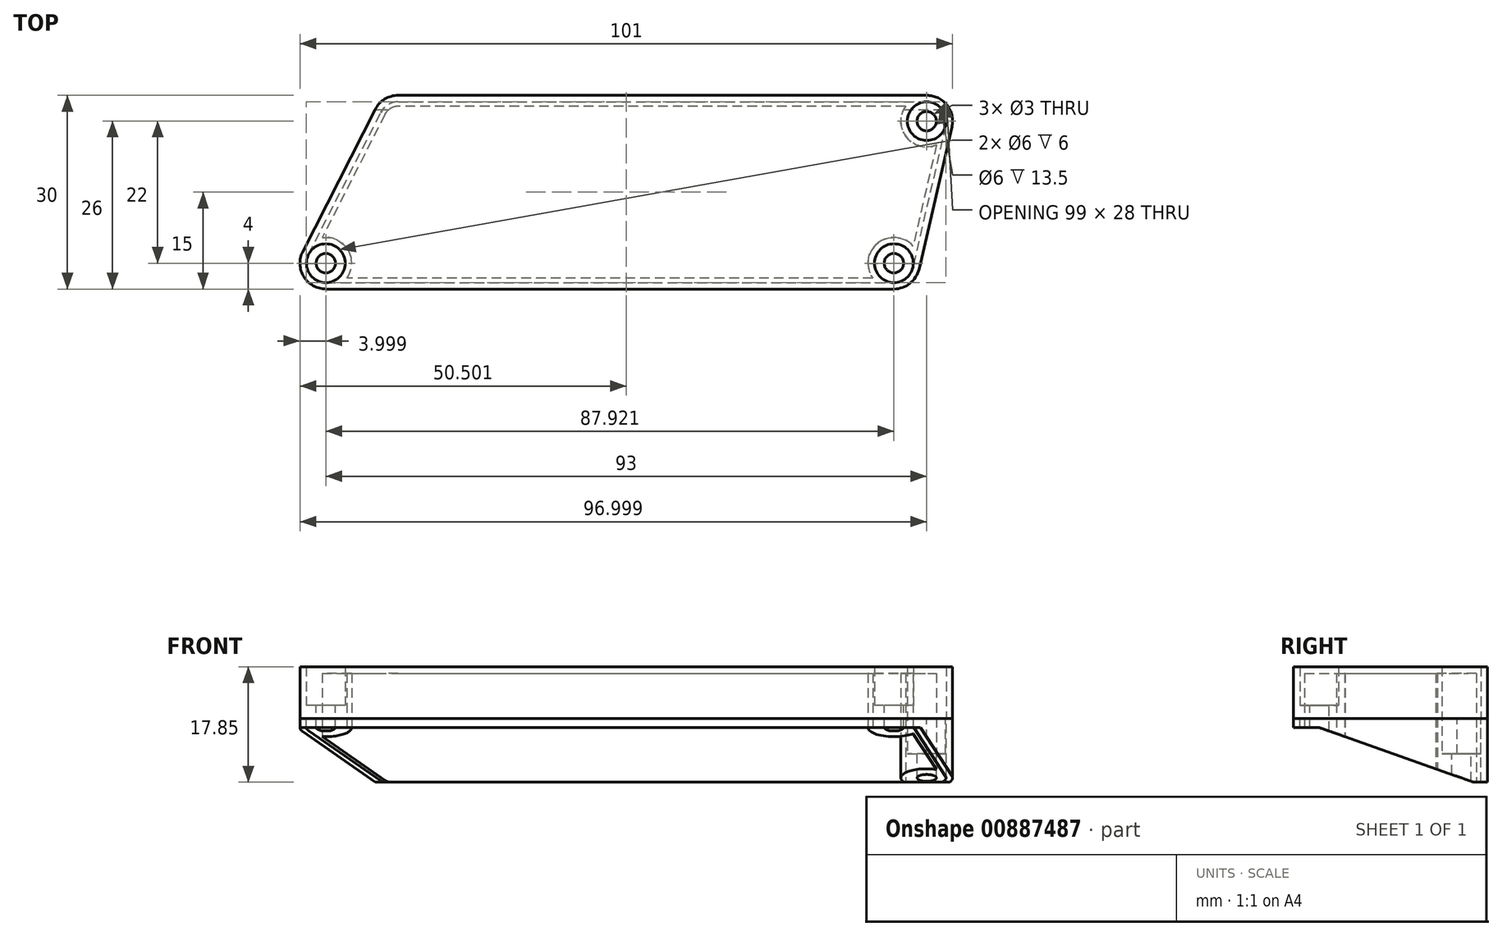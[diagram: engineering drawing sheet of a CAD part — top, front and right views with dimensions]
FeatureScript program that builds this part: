
annotation { "Feature Type Name" : "Feature", "Feature Type Description" : "" }
export const myFeature = defineFeature(function(context is Context, id is Id, definition is map)
    precondition{}
    {
        {
            var Q0;
            Q0=qCreatedBy(makeId("Top.planeOp"),FACE);
            var sketch = newSketch(context, id + "F0", { "sketchPlane" : qUnion([Q0])});
            skLineSegment(sketch, "E0.bottom", {"start": v(52.28, -15) * mm, "end": v(-52.28, -15) * mm, "construction": true});
            skLineSegment(sketch, "E0.top", {"start": v(52.28, 15) * mm, "end": v(-52.28, 15) * mm, "construction": true});
            skLineSegment(sketch, "E0.left", {"start": v(52.28, -15) * mm, "end": v(52.28, 15) * mm, "construction": true});
            skLineSegment(sketch, "E0.right", {"start": v(-52.28, -15) * mm, "end": v(-52.28, 15) * mm, "construction": true});
            skPoint(sketch, "E0.middle", {"position": v(0, 0) * mm});
            skLineSegment(sketch, "E1", {"start": v(-52.28, -15) * mm, "end": v(-37, 15) * mm});
            skLineSegment(sketch, "E2", {"start": v(52.28, 15) * mm, "end": v(45.35, -15) * mm});
            skLineSegment(sketch, "E3", {"start": v(-37, 15) * mm, "end": v(52.28, 15) * mm});
            skLineSegment(sketch, "E4", {"start": v(45.35, -15) * mm, "end": v(-52.28, -15) * mm});
            skCircle(sketch, "E5", {"center": v(-45.75, -11) * mm, "radius": 3 * mm});
            skCircle(sketch, "E6", {"center": v(-45.75, -11) * mm, "radius": 4 * mm});
            skCircle(sketch, "E7", {"center": v(-45.75, -11) * mm, "radius": 1.5 * mm});
            skCircle(sketch, "E8", {"center": v(-34.54, 11) * mm, "radius": 3 * mm});
            skCircle(sketch, "E9", {"center": v(-34.54, 11) * mm, "radius": 4 * mm});
            skCircle(sketch, "E10", {"center": v(-34.54, 11) * mm, "radius": 1.5 * mm});
            skCircle(sketch, "E11", {"center": v(47.25, 11) * mm, "radius": 3 * mm});
            skCircle(sketch, "E12", {"center": v(47.25, 11) * mm, "radius": 4 * mm});
            skCircle(sketch, "E13", {"center": v(47.25, 11) * mm, "radius": 1.5 * mm});
            skCircle(sketch, "E14", {"center": v(42.17, -11) * mm, "radius": 3 * mm});
            skCircle(sketch, "E15", {"center": v(42.17, -11) * mm, "radius": 4 * mm});
            skCircle(sketch, "E16", {"center": v(42.17, -11) * mm, "radius": 1.5 * mm});
            skLineSegment(sketch, "E17", {"start": v(50.17, 10.33) * mm, "end": v(45.1, -11.67) * mm});
            skLineSegment(sketch, "E18", {"start": v(-45.75, -14) * mm, "end": v(42.17, -14) * mm});
            skLineSegment(sketch, "E19", {"start": v(-48.42, -9.64) * mm, "end": v(-37.21, 12.36) * mm});
            skLineSegment(sketch, "E20", {"start": v(-34.54, 14) * mm, "end": v(47.25, 14) * mm});
            skLineSegment(sketch, "E21", {"start": v(-42.48, -13.3) * mm, "end": v(38.9, -13.3) * mm});
            skLineSegment(sketch, "E22", {"start": v(45.15, -8.33) * mm, "end": v(48.75, 7.3) * mm});
            skLineSegment(sketch, "E23", {"start": v(-31.27, 13.3) * mm, "end": v(43.98, 13.3) * mm});
            skLineSegment(sketch, "E24", {"start": v(-46.31, -7.04) * mm, "end": v(-38.08, 9.13) * mm});
            skLineSegment(sketch, "E25", {"start": v(-38.08, 9.13) * mm, "end": v(-37.46, 10.33) * mm});
            skLineSegment(sketch, "E26", {"start": v(-31.27, 13.3) * mm, "end": v(-32.61, 13.3) * mm});
            skLineSegment(sketch, "E27", {"start": v(43.98, 13.3) * mm, "end": v(45.32, 13.3) * mm});
            skLineSegment(sketch, "E28", {"start": v(48.75, 7.3) * mm, "end": v(49.06, 8.6) * mm});
            skLineSegment(sketch, "E29", {"start": v(45.15, -8.33) * mm, "end": v(44.84, -9.64) * mm});
            skLineSegment(sketch, "E30", {"start": v(38.9, -13.3) * mm, "end": v(40.24, -13.3) * mm});
            skLineSegment(sketch, "E31", {"start": v(-42.48, -13.3) * mm, "end": v(-43.82, -13.3) * mm});
            skLineSegment(sketch, "E32", {"start": v(-46.31, -7.04) * mm, "end": v(-46.93, -8.24) * mm});
            skLineSegment(sketch, "E33", {"start": v(-37.46, 10.33) * mm, "end": v(-35.95, 13.3) * mm});
            skLineSegment(sketch, "E34", {"start": v(-35.95, 13.3) * mm, "end": v(-32.61, 13.3) * mm});
            skCircle(sketch, "E35", {"center": v(-34.54, 11) * mm, "radius": 2.3 * mm});
            skLineSegment(sketch, "E36", {"start": v(-49.75, -15) * mm, "end": v(-49.75, 15) * mm, "construction": true});
            skLineSegment(sketch, "E37", {"start": v(51.25, 15) * mm, "end": v(51.25, -15) * mm, "construction": true});
            skSolve(sketch);
        }
        {
            var Q0;
            {var subQ2=sQuery(id+"F0.wireOp",EDGE,"E17");var subQ7=sQuery(id+"F0.wireOp",EDGE,"E14");var subQ8=makeQuery(id+"F0.imprint","INTERSECT",VERTEX,{"derivedFrom":[subQ7,subQ2]});Q0=makeQuery(id+"F0.imprint","IMPRINT",FACE,{"disambiguationData":[TD([[makeQuery(id+"F0.imprint","IMPRINT",EDGE,{"disambiguationData":[TD([[subQ8,1.0]])],"derivedFrom":subQ7}),-1.0]])]});}
            var Q1;
            {var subQ5=sQuery(id+"F0.wireOp",EDGE,"E14");var subQ7=sQuery(id+"F0.wireOp",EDGE,"E17");var subQ9=makeQuery(id+"F0.imprint","INTERSECT",VERTEX,{"derivedFrom":[subQ5,subQ7]});Q1=makeQuery(id+"F0.imprint","IMPRINT",FACE,{"disambiguationData":[TD([[makeQuery(id+"F0.imprint","IMPRINT",EDGE,{"disambiguationData":[TD([[subQ9,-1.0]])],"derivedFrom":subQ5}),-1.0]])]});}
            var Q2;
            Q2=makeQuery(id+"F0.imprint","IMPRINT",FACE,{"disambiguationData":[TD([[makeQuery(id+"F0.imprint","IMPRINT",EDGE,{"derivedFrom":sQuery(id+"F0.wireOp",EDGE,"E16")}),-1.0]])]});
            var Q3;
            Q3=makeQuery(id+"F0.imprint","IMPRINT",FACE,{"disambiguationData":[TD([[makeQuery(id+"F0.imprint","IMPRINT",EDGE,{"derivedFrom":sQuery(id+"F0.wireOp",EDGE,"E13")}),-1.0]])]});
            var Q4;
            {var subQ0=sQuery(id+"F0.wireOp",EDGE,"E6");var subQ1=sQuery(id+"F0.wireOp",EDGE,"E1");var subQ2=makeQuery(id+"F0.imprint","INTERSECT",VERTEX,{"derivedFrom":[subQ1,subQ0]});Q4=makeQuery(id+"F0.imprint","IMPRINT",FACE,{"disambiguationData":[TD([[makeQuery(id+"F0.imprint","IMPRINT",EDGE,{"disambiguationData":[TD([[subQ2,-1.0]])],"derivedFrom":subQ1}),-1.0]])]});}
            var Q5;
            {var subQ0=sQuery(id+"F0.wireOp",EDGE,"E9");var subQ1=sQuery(id+"F0.wireOp",EDGE,"E3");var subQ2=makeQuery(id+"F0.imprint","INTERSECT",VERTEX,{"derivedFrom":[subQ1,subQ0]});Q5=makeQuery(id+"F0.imprint","IMPRINT",FACE,{"disambiguationData":[TD([[makeQuery(id+"F0.imprint","IMPRINT",EDGE,{"disambiguationData":[TD([[subQ2,-1.0]])],"derivedFrom":subQ1}),-1.0]])]});}
            var Q6;
            {var subQ0=sQuery(id+"F0.wireOp",EDGE,"E12");var subQ1=sQuery(id+"F0.wireOp",EDGE,"E2");var subQ2=makeQuery(id+"F0.imprint","INTERSECT",VERTEX,{"derivedFrom":[subQ1,subQ0]});Q6=makeQuery(id+"F0.imprint","IMPRINT",FACE,{"disambiguationData":[TD([[makeQuery(id+"F0.imprint","IMPRINT",EDGE,{"disambiguationData":[TD([[subQ2,-1.0]])],"derivedFrom":subQ1}),-1.0]])]});}
            var Q7;
            {var subQ0=sQuery(id+"F0.wireOp",EDGE,"E22");Q7=makeQuery(id+"F0.imprint","IMPRINT",FACE,{"disambiguationData":[TD([[makeQuery(id+"F0.imprint","IMPRINT",EDGE,{"derivedFrom":subQ0}),-1.0]])]});}
            var Q8;
            {var subQ0=sQuery(id+"F0.wireOp",EDGE,"E24");Q8=makeQuery(id+"F0.imprint","IMPRINT",FACE,{"disambiguationData":[TD([[makeQuery(id+"F0.imprint","IMPRINT",EDGE,{"derivedFrom":subQ0}),1.0]])]});}
            var Q9;
            Q9=makeQuery(id+"F0.imprint","IMPRINT",FACE,{"disambiguationData":[TD([[makeQuery(id+"F0.imprint","IMPRINT",EDGE,{"derivedFrom":sQuery(id+"F0.wireOp",EDGE,"E16")}),1.0]])]});
            var Q10;
            Q10=makeQuery(id+"F0.imprint","IMPRINT",FACE,{"disambiguationData":[TD([[makeQuery(id+"F0.imprint","IMPRINT",EDGE,{"derivedFrom":sQuery(id+"F0.wireOp",EDGE,"E13")}),1.0]])]});
            var Q11;
            {var subQ5=sQuery(id+"F0.wireOp",EDGE,"E18");var subQ7=sQuery(id+"F0.wireOp",EDGE,"E5");var subQ8=makeQuery(id+"F0.imprint","INTERSECT",VERTEX,{"derivedFrom":[subQ7,subQ5]});Q11=makeQuery(id+"F0.imprint","IMPRINT",FACE,{"disambiguationData":[TD([[makeQuery(id+"F0.imprint","IMPRINT",EDGE,{"disambiguationData":[TD([[subQ8,1.0]])],"derivedFrom":subQ7}),-1.0]])]});}
            var Q12;
            Q12=makeQuery(id+"F0.imprint","IMPRINT",FACE,{"disambiguationData":[TD([[makeQuery(id+"F0.imprint","IMPRINT",EDGE,{"derivedFrom":sQuery(id+"F0.wireOp",EDGE,"E7")}),-1.0]])]});
            var Q13;
            Q13=makeQuery(id+"F0.imprint","IMPRINT",FACE,{"disambiguationData":[TD([[makeQuery(id+"F0.imprint","IMPRINT",EDGE,{"derivedFrom":sQuery(id+"F0.wireOp",EDGE,"E7")}),1.0]])]});
            var Q14;
            {var subQ5=sQuery(id+"F0.wireOp",EDGE,"E18");var subQ7=sQuery(id+"F0.wireOp",EDGE,"E5");var subQ8=makeQuery(id+"F0.imprint","INTERSECT",VERTEX,{"derivedFrom":[subQ7,subQ5]});Q14=makeQuery(id+"F0.imprint","IMPRINT",FACE,{"disambiguationData":[TD([[makeQuery(id+"F0.imprint","IMPRINT",EDGE,{"disambiguationData":[TD([[subQ8,-1.0]])],"derivedFrom":subQ7}),-1.0]])]});}
            var Q15;
            {var subQ0=sQuery(id+"F0.wireOp",EDGE,"E21");Q15=makeQuery(id+"F0.imprint","IMPRINT",FACE,{"disambiguationData":[TD([[makeQuery(id+"F0.imprint","IMPRINT",EDGE,{"derivedFrom":subQ0}),-1.0]])]});}
            var Q16;
            {var subQ0=sQuery(id+"F0.wireOp",EDGE,"E15");var subQ1=sQuery(id+"F0.wireOp",EDGE,"E4");var subQ2=makeQuery(id+"F0.imprint","INTERSECT",VERTEX,{"derivedFrom":[subQ1,subQ0]});Q16=makeQuery(id+"F0.imprint","IMPRINT",FACE,{"disambiguationData":[TD([[makeQuery(id+"F0.imprint","IMPRINT",EDGE,{"disambiguationData":[TD([[subQ2,-1.0]])],"derivedFrom":subQ1}),-1.0]])]});}
            var Q17;
            {var subQ5=sQuery(id+"F0.wireOp",EDGE,"E19");var subQ6=sQuery(id+"F0.wireOp",EDGE,"E8");var subQ7=makeQuery(id+"F0.imprint","INTERSECT",VERTEX,{"derivedFrom":[subQ6,subQ5]});Q17=makeQuery(id+"F0.imprint","IMPRINT",FACE,{"disambiguationData":[TD([[makeQuery(id+"F0.imprint","IMPRINT",EDGE,{"disambiguationData":[TD([[subQ7,-1.0]])],"derivedFrom":subQ6}),-1.0]])]});}
            var Q18;
            {var subQ5=sQuery(id+"F0.wireOp",EDGE,"E17");var subQ7=sQuery(id+"F0.wireOp",EDGE,"E11");var subQ8=makeQuery(id+"F0.imprint","INTERSECT",VERTEX,{"derivedFrom":[subQ7,subQ5]});Q18=makeQuery(id+"F0.imprint","IMPRINT",FACE,{"disambiguationData":[TD([[makeQuery(id+"F0.imprint","IMPRINT",EDGE,{"disambiguationData":[TD([[subQ8,1.0]])],"derivedFrom":subQ7}),-1.0]])]});}
            var Q19;
            {var subQ3=sQuery(id+"F0.wireOp",EDGE,"E17");var subQ4=sQuery(id+"F0.wireOp",EDGE,"E11");var subQ5=makeQuery(id+"F0.imprint","INTERSECT",VERTEX,{"derivedFrom":[subQ4,subQ3]});Q19=makeQuery(id+"F0.imprint","IMPRINT",FACE,{"disambiguationData":[TD([[makeQuery(id+"F0.imprint","IMPRINT",EDGE,{"disambiguationData":[TD([[subQ5,-1.0]])],"derivedFrom":subQ4}),-1.0]])]});}
            var Q20;
            {var subQ5=sQuery(id+"F0.wireOp",EDGE,"E8");var subQ7=sQuery(id+"F0.wireOp",EDGE,"E19");var subQ9=makeQuery(id+"F0.imprint","INTERSECT",VERTEX,{"derivedFrom":[subQ5,subQ7]});Q20=makeQuery(id+"F0.imprint","IMPRINT",FACE,{"disambiguationData":[TD([[makeQuery(id+"F0.imprint","IMPRINT",EDGE,{"disambiguationData":[TD([[subQ9,1.0]])],"derivedFrom":subQ5}),-1.0]])]});}
            var Q21;
            {var subQ0=sQuery(id+"F0.wireOp",EDGE,"E23");Q21=makeQuery(id+"F0.imprint","IMPRINT",FACE,{"disambiguationData":[TD([[makeQuery(id+"F0.imprint","IMPRINT",EDGE,{"derivedFrom":subQ0}),1.0]])]});}
            var Q22;
            {var subQ3=sQuery(id+"F0.wireOp",EDGE,"E26");Q22=makeQuery(id+"F0.imprint","IMPRINT",FACE,{"disambiguationData":[TD([[makeQuery(id+"F0.imprint","IMPRINT",EDGE,{"derivedFrom":subQ3}),-1.0]])]});}
            var Q23;
            {var subQ3=sQuery(id+"F0.wireOp",EDGE,"E32");Q23=makeQuery(id+"F0.imprint","IMPRINT",FACE,{"disambiguationData":[TD([[makeQuery(id+"F0.imprint","IMPRINT",EDGE,{"derivedFrom":subQ3}),-1.0]])]});}
            var Q24;
            {var subQ0=sQuery(id+"F0.wireOp",EDGE,"E31");Q24=makeQuery(id+"F0.imprint","IMPRINT",FACE,{"disambiguationData":[TD([[makeQuery(id+"F0.imprint","IMPRINT",EDGE,{"derivedFrom":subQ0}),-1.0]])]});}
            var Q25;
            {var subQ0=sQuery(id+"F0.wireOp",EDGE,"E27");Q25=makeQuery(id+"F0.imprint","IMPRINT",FACE,{"disambiguationData":[TD([[makeQuery(id+"F0.imprint","IMPRINT",EDGE,{"derivedFrom":subQ0}),-1.0]])]});}
            var Q26;
            {var subQ3=sQuery(id+"F0.wireOp",EDGE,"E27");Q26=makeQuery(id+"F0.imprint","IMPRINT",FACE,{"disambiguationData":[TD([[makeQuery(id+"F0.imprint","IMPRINT",EDGE,{"derivedFrom":subQ3}),1.0]])]});}
            var Q27;
            {var subQ0=sQuery(id+"F0.wireOp",EDGE,"E29");Q27=makeQuery(id+"F0.imprint","IMPRINT",FACE,{"disambiguationData":[TD([[makeQuery(id+"F0.imprint","IMPRINT",EDGE,{"derivedFrom":subQ0}),-1.0]])]});}
            var Q28;
            {var subQ3=sQuery(id+"F0.wireOp",EDGE,"E30");Q28=makeQuery(id+"F0.imprint","IMPRINT",FACE,{"disambiguationData":[TD([[makeQuery(id+"F0.imprint","IMPRINT",EDGE,{"derivedFrom":subQ3}),-1.0]])]});}
            var Q29;
            {var subQ1=sQuery(id+"F0.wireOp",EDGE,"E8");var subQ5=makeQuery(id+"F0.imprint","INTERSECT",VERTEX,{"derivedFrom":[subQ1,sQuery(id+"F0.wireOp",EDGE,"E19")]});Q29=makeQuery(id+"F0.imprint","IMPRINT",FACE,{"disambiguationData":[TD([[makeQuery(id+"F0.imprint","IMPRINT",EDGE,{"disambiguationData":[TD([[subQ5,1.0]])],"derivedFrom":subQ1}),1.0]])]});}
            var Q30;
            {var subQ0=sQuery(id+"F0.wireOp",EDGE,"E34");var subQ1=sQuery(id+"F0.wireOp",EDGE,"E33");var subQ2=makeQuery(id+"F0.imprint","INTERSECT",VERTEX,{"derivedFrom":[subQ1,subQ0]});Q30=makeQuery(id+"F0.imprint","IMPRINT",FACE,{"disambiguationData":[TD([[makeQuery(id+"F0.imprint","IMPRINT",EDGE,{"disambiguationData":[TD([[subQ2,1.0]])],"derivedFrom":subQ1}),-1.0]])]});}
            extrude(context, id + "F1", {"entities" : qUnion([Q0, Q1, Q2, Q3, Q4, Q5, Q6, Q7, Q8, Q9, Q10, Q11, Q12, Q13, Q14, Q15, Q16, Q17, Q18, Q19, Q20, Q21, Q22, Q23, Q24, Q25, Q26, Q27, Q28, Q29, Q30]), "depth" : 8 * mm, "offsetDistance" : 25 * mm});
        }
        {
            var Q0;
            {var subQ0=sQuery(id+"F0.wireOp",EDGE,"E21");Q0=makeQuery(id+"F0.imprint","IMPRINT",FACE,{"disambiguationData":[TD([[makeQuery(id+"F0.imprint","IMPRINT",EDGE,{"derivedFrom":subQ0}),1.0]])]});}
            var Q1;
            {var subQ0=sQuery(id+"F0.wireOp",EDGE,"E33");var subQ5=sQuery(id+"F0.wireOp",EDGE,"E35");var subQ6=makeQuery(id+"F0.imprint","INTERSECT",VERTEX,{"derivedFrom":[subQ0,subQ5]});Q1=makeQuery(id+"F0.imprint","IMPRINT",FACE,{"disambiguationData":[TD([[makeQuery(id+"F0.imprint","IMPRINT",EDGE,{"disambiguationData":[TD([[subQ6,-1.0]])],"derivedFrom":subQ5}),-1.0]])]});}
            var Q2;
            Q2=makeQuery(id+"F0.imprint","IMPRINT",FACE,{"disambiguationData":[TD([[makeQuery(id+"F0.imprint","IMPRINT",EDGE,{"derivedFrom":sQuery(id+"F0.wireOp",EDGE,"E10")}),-1.0]])]});
            var Q3;
            Q3=makeQuery(id+"F0.imprint","IMPRINT",FACE,{"disambiguationData":[TD([[makeQuery(id+"F0.imprint","IMPRINT",EDGE,{"derivedFrom":sQuery(id+"F0.wireOp",EDGE,"E10")}),1.0]])]});
            var Q4;
            {var subQ0=sQuery(id+"F0.wireOp",EDGE,"E25");Q4=makeQuery(id+"F0.imprint","IMPRINT",FACE,{"disambiguationData":[TD([[makeQuery(id+"F0.imprint","IMPRINT",EDGE,{"derivedFrom":subQ0}),-1.0]])]});}
            extrude(context, id + "F2", {"entities" : qUnion([Q0, Q1, Q2, Q3, Q4]), "operationType" : NewBodyOperationType.ADD, "depth" : 8 * mm, "offsetDistance" : 25 * mm, "hasSecondDirection" : true, "secondDirectionOppositeDirection" : false, "secondDirectionDepth" : 7 * mm});
        }
        {
            var Q0;
            {var subQ4=sQuery(id+"F0.wireOp",EDGE,"E14");var subQ7=sQuery(id+"F0.wireOp",EDGE,"E17");var subQ9=makeQuery(id+"F0.imprint","INTERSECT",VERTEX,{"derivedFrom":[subQ4,subQ7]});Q0=makeQuery(id+"F0.imprint","IMPRINT",FACE,{"disambiguationData":[TD([[makeQuery(id+"F0.imprint","IMPRINT",EDGE,{"disambiguationData":[TD([[subQ9,-1.0]])],"derivedFrom":subQ4}),-1.0]])]});}
            var Q1;
            {var subQ0=sQuery(id+"F0.wireOp",EDGE,"E9");var subQ6=sQuery(id+"F0.wireOp",EDGE,"sEmSDasX-VnLR-kRRF-FZfv-y3YDyhKKrgE7");var subQ8=makeQuery(id+"F0.imprint","INTERSECT",VERTEX,{"disambiguationData":[OD(0.0)],"derivedFrom":[subQ6,subQ0]});Q1=makeQuery(id+"F0.imprint","IMPRINT",FACE,{"disambiguationData":[TD([[makeQuery(id+"F0.imprint","IMPRINT",EDGE,{"disambiguationData":[TD([[subQ8,-1.0]])],"derivedFrom":subQ6}),1.0]])]});}
            var Q2;
            {var subQ0=sQuery(id+"F0.wireOp",EDGE,"E9");var subQ2=sQuery(id+"F0.wireOp",EDGE,"sEmSDasX-VnLR-kRRF-FZfv-y3YDyhKKrgE7");var subQ3=makeQuery(id+"F0.imprint","INTERSECT",VERTEX,{"disambiguationData":[OD(0.0)],"derivedFrom":[subQ2,subQ0]});Q2=makeQuery(id+"F0.imprint","IMPRINT",FACE,{"disambiguationData":[TD([[makeQuery(id+"F0.imprint","IMPRINT",EDGE,{"disambiguationData":[TD([[subQ3,-1.0]])],"derivedFrom":subQ2}),-1.0]])]});}
            var Q3;
            {var subQ0=sQuery(id+"F0.wireOp",EDGE,"E6");var subQ2=sQuery(id+"F0.wireOp",EDGE,"s6BABxoF-F3zb-I8wc-I3Xw-FraqOPEOQCRA");var subQ3=makeQuery(id+"F0.imprint","INTERSECT",VERTEX,{"disambiguationData":[OD(0.0)],"derivedFrom":[subQ2,subQ0]});Q3=makeQuery(id+"F0.imprint","IMPRINT",FACE,{"disambiguationData":[TD([[makeQuery(id+"F0.imprint","IMPRINT",EDGE,{"disambiguationData":[TD([[subQ3,-1.0]])],"derivedFrom":subQ2}),-1.0]])]});}
            var Q4;
            {var subQ0=sQuery(id+"F0.wireOp",EDGE,"E6");var subQ2=sQuery(id+"F0.wireOp",EDGE,"s6BABxoF-F3zb-I8wc-I3Xw-FraqOPEOQCRA");var subQ3=makeQuery(id+"F0.imprint","INTERSECT",VERTEX,{"disambiguationData":[OD(0.0)],"derivedFrom":[subQ2,subQ0]});Q4=makeQuery(id+"F0.imprint","IMPRINT",FACE,{"disambiguationData":[TD([[makeQuery(id+"F0.imprint","IMPRINT",EDGE,{"disambiguationData":[TD([[subQ3,-1.0]])],"derivedFrom":subQ2}),1.0]])]});}
            var Q5;
            {var subQ0=sQuery(id+"F0.wireOp",EDGE,"E12");var subQ3=sQuery(id+"F0.wireOp",EDGE,"MlNcj02m-OnEw-u7mJ-xsQt-vaGhrOIsEcpA");var subQ4=makeQuery(id+"F0.imprint","INTERSECT",VERTEX,{"disambiguationData":[OD(0.0)],"derivedFrom":[subQ3,subQ0]});Q5=makeQuery(id+"F0.imprint","IMPRINT",FACE,{"disambiguationData":[TD([[makeQuery(id+"F0.imprint","IMPRINT",EDGE,{"disambiguationData":[TD([[subQ4,-1.0]])],"derivedFrom":subQ3}),-1.0]])]});}
            var Q6;
            {var subQ0=sQuery(id+"F0.wireOp",EDGE,"E12");var subQ1=sQuery(id+"F0.wireOp",EDGE,"MlNcj02m-OnEw-u7mJ-xsQt-vaGhrOIsEcpA");var subQ2=makeQuery(id+"F0.imprint","INTERSECT",VERTEX,{"disambiguationData":[OD(0.0)],"derivedFrom":[subQ1,subQ0]});Q6=makeQuery(id+"F0.imprint","IMPRINT",FACE,{"disambiguationData":[TD([[makeQuery(id+"F0.imprint","IMPRINT",EDGE,{"disambiguationData":[TD([[subQ2,-1.0]])],"derivedFrom":subQ1}),1.0]])]});}
            var Q7;
            {var subQ0=sQuery(id+"F0.wireOp",EDGE,"E5");var subQ2=sQuery(id+"F0.wireOp",EDGE,"s6BABxoF-F3zb-I8wc-I3Xw-FraqOPEOQCRA");var subQ7=makeQuery(id+"F0.imprint","INTERSECT",VERTEX,{"disambiguationData":[OD(0.0)],"derivedFrom":[subQ2,subQ0]});Q7=makeQuery(id+"F0.imprint","IMPRINT",FACE,{"disambiguationData":[TD([[makeQuery(id+"F0.imprint","IMPRINT",EDGE,{"disambiguationData":[TD([[subQ7,-1.0]])],"derivedFrom":subQ2}),1.0]])]});}
            var Q8;
            {var subQ0=sQuery(id+"F0.wireOp",EDGE,"E5");var subQ2=sQuery(id+"F0.wireOp",EDGE,"s6BABxoF-F3zb-I8wc-I3Xw-FraqOPEOQCRA");var subQ7=makeQuery(id+"F0.imprint","INTERSECT",VERTEX,{"disambiguationData":[OD(0.0)],"derivedFrom":[subQ2,subQ0]});Q8=makeQuery(id+"F0.imprint","IMPRINT",FACE,{"disambiguationData":[TD([[makeQuery(id+"F0.imprint","IMPRINT",EDGE,{"disambiguationData":[TD([[subQ7,-1.0]])],"derivedFrom":subQ2}),-1.0]])]});}
            var Q9;
            {var subQ0=sQuery(id+"F0.wireOp",EDGE,"E8");var subQ2=sQuery(id+"F0.wireOp",EDGE,"sEmSDasX-VnLR-kRRF-FZfv-y3YDyhKKrgE7");var subQ4=makeQuery(id+"F0.imprint","INTERSECT",VERTEX,{"disambiguationData":[OD(0.0)],"derivedFrom":[subQ2,subQ0]});Q9=makeQuery(id+"F0.imprint","IMPRINT",FACE,{"disambiguationData":[TD([[makeQuery(id+"F0.imprint","IMPRINT",EDGE,{"disambiguationData":[TD([[subQ4,-1.0]])],"derivedFrom":subQ2}),-1.0]])]});}
            var Q10;
            {var subQ0=sQuery(id+"F0.wireOp",EDGE,"E8");var subQ2=sQuery(id+"F0.wireOp",EDGE,"sEmSDasX-VnLR-kRRF-FZfv-y3YDyhKKrgE7");var subQ3=makeQuery(id+"F0.imprint","INTERSECT",VERTEX,{"disambiguationData":[OD(0.0)],"derivedFrom":[subQ2,subQ0]});Q10=makeQuery(id+"F0.imprint","IMPRINT",FACE,{"disambiguationData":[TD([[makeQuery(id+"F0.imprint","IMPRINT",EDGE,{"disambiguationData":[TD([[subQ3,-1.0]])],"derivedFrom":subQ2}),1.0]])]});}
            var Q11;
            {var subQ0=sQuery(id+"F0.wireOp",EDGE,"E11");var subQ1=sQuery(id+"F0.wireOp",EDGE,"MlNcj02m-OnEw-u7mJ-xsQt-vaGhrOIsEcpA");var subQ2=makeQuery(id+"F0.imprint","INTERSECT",VERTEX,{"disambiguationData":[OD(0.0)],"derivedFrom":[subQ1,subQ0]});Q11=makeQuery(id+"F0.imprint","IMPRINT",FACE,{"disambiguationData":[TD([[makeQuery(id+"F0.imprint","IMPRINT",EDGE,{"disambiguationData":[TD([[subQ2,-1.0]])],"derivedFrom":subQ1}),1.0]])]});}
            var Q12;
            {var subQ0=sQuery(id+"F0.wireOp",EDGE,"E23");var subQ1=sQuery(id+"F0.wireOp",EDGE,"MlNcj02m-OnEw-u7mJ-xsQt-vaGhrOIsEcpA");var subQ2=makeQuery(id+"F0.imprint","INTERSECT",VERTEX,{"derivedFrom":[subQ1,subQ0]});Q12=makeQuery(id+"F0.imprint","IMPRINT",FACE,{"disambiguationData":[TD([[makeQuery(id+"F0.imprint","IMPRINT",EDGE,{"disambiguationData":[TD([[subQ2,-1.0]])],"derivedFrom":subQ1}),-1.0]])]});}
            var Q13;
            {var subQ0=sQuery(id+"F0.wireOp",EDGE,"E21");var subQ1=sQuery(id+"F0.wireOp",EDGE,"dffKxZ2D-OvlK-9A7r-lY4j-voeP4siTT3Bg");var subQ2=makeQuery(id+"F0.imprint","INTERSECT",VERTEX,{"derivedFrom":[subQ1,subQ0]});Q13=makeQuery(id+"F0.imprint","IMPRINT",FACE,{"disambiguationData":[TD([[makeQuery(id+"F0.imprint","IMPRINT",EDGE,{"disambiguationData":[TD([[subQ2,-1.0]])],"derivedFrom":subQ1}),-1.0]])]});}
            var Q14;
            {var subQ0=sQuery(id+"F0.wireOp",EDGE,"E21");var subQ1=sQuery(id+"F0.wireOp",EDGE,"dffKxZ2D-OvlK-9A7r-lY4j-voeP4siTT3Bg");var subQ2=makeQuery(id+"F0.imprint","INTERSECT",VERTEX,{"derivedFrom":[subQ1,subQ0]});Q14=makeQuery(id+"F0.imprint","IMPRINT",FACE,{"disambiguationData":[TD([[makeQuery(id+"F0.imprint","IMPRINT",EDGE,{"disambiguationData":[TD([[subQ2,-1.0]])],"derivedFrom":subQ1}),1.0]])]});}
            var Q15;
            {var subQ0=sQuery(id+"F0.wireOp",EDGE,"E22");Q15=makeQuery(id+"F0.imprint","IMPRINT",FACE,{"disambiguationData":[TD([[makeQuery(id+"F0.imprint","IMPRINT",EDGE,{"derivedFrom":subQ0}),-1.0]])]});}
            var Q16;
            {var subQ1=sQuery(id+"F0.wireOp",EDGE,"MlNcj02m-OnEw-u7mJ-xsQt-vaGhrOIsEcpA");var subQ5=sQuery(id+"F0.wireOp",EDGE,"E23");var subQ9=makeQuery(id+"F0.imprint","INTERSECT",VERTEX,{"derivedFrom":[subQ1,subQ5]});Q16=makeQuery(id+"F0.imprint","IMPRINT",FACE,{"disambiguationData":[TD([[makeQuery(id+"F0.imprint","IMPRINT",EDGE,{"disambiguationData":[TD([[subQ9,-1.0]])],"derivedFrom":subQ1}),1.0]])]});}
            var Q17;
            {var subQ0=sQuery(id+"F0.wireOp",EDGE,"E24");Q17=makeQuery(id+"F0.imprint","IMPRINT",FACE,{"disambiguationData":[TD([[makeQuery(id+"F0.imprint","IMPRINT",EDGE,{"derivedFrom":subQ0}),1.0]])]});}
            var Q18;
            {var subQ0=sQuery(id+"F0.wireOp",EDGE,"E7");var subQ1=sQuery(id+"F0.wireOp",EDGE,"s6BABxoF-F3zb-I8wc-I3Xw-FraqOPEOQCRA");var subQ2=makeQuery(id+"F0.imprint","INTERSECT",VERTEX,{"disambiguationData":[OD(0.0)],"derivedFrom":[subQ1,subQ0]});Q18=makeQuery(id+"F0.imprint","IMPRINT",FACE,{"disambiguationData":[TD([[makeQuery(id+"F0.imprint","IMPRINT",EDGE,{"disambiguationData":[TD([[subQ2,-1.0]])],"derivedFrom":subQ1}),1.0]])]});}
            var Q19;
            {var subQ0=sQuery(id+"F0.wireOp",EDGE,"E7");var subQ1=sQuery(id+"F0.wireOp",EDGE,"s6BABxoF-F3zb-I8wc-I3Xw-FraqOPEOQCRA");var subQ2=makeQuery(id+"F0.imprint","INTERSECT",VERTEX,{"disambiguationData":[OD(0.0)],"derivedFrom":[subQ1,subQ0]});Q19=makeQuery(id+"F0.imprint","IMPRINT",FACE,{"disambiguationData":[TD([[makeQuery(id+"F0.imprint","IMPRINT",EDGE,{"disambiguationData":[TD([[subQ2,-1.0]])],"derivedFrom":subQ1}),-1.0]])]});}
            var Q20;
            {var subQ0=sQuery(id+"F0.wireOp",EDGE,"E10");var subQ1=sQuery(id+"F0.wireOp",EDGE,"sEmSDasX-VnLR-kRRF-FZfv-y3YDyhKKrgE7");var subQ2=makeQuery(id+"F0.imprint","INTERSECT",VERTEX,{"disambiguationData":[OD(0.0)],"derivedFrom":[subQ1,subQ0]});Q20=makeQuery(id+"F0.imprint","IMPRINT",FACE,{"disambiguationData":[TD([[makeQuery(id+"F0.imprint","IMPRINT",EDGE,{"disambiguationData":[TD([[subQ2,-1.0]])],"derivedFrom":subQ1}),1.0]])]});}
            var Q21;
            {var subQ0=sQuery(id+"F0.wireOp",EDGE,"E10");var subQ1=sQuery(id+"F0.wireOp",EDGE,"sEmSDasX-VnLR-kRRF-FZfv-y3YDyhKKrgE7");var subQ2=makeQuery(id+"F0.imprint","INTERSECT",VERTEX,{"disambiguationData":[OD(0.0)],"derivedFrom":[subQ1,subQ0]});Q21=makeQuery(id+"F0.imprint","IMPRINT",FACE,{"disambiguationData":[TD([[makeQuery(id+"F0.imprint","IMPRINT",EDGE,{"disambiguationData":[TD([[subQ2,-1.0]])],"derivedFrom":subQ1}),-1.0]])]});}
            var Q22;
            Q22=makeQuery(id+"F0.imprint","IMPRINT",FACE,{"disambiguationData":[TD([[makeQuery(id+"F0.imprint","IMPRINT",EDGE,{"derivedFrom":sQuery(id+"F0.wireOp",EDGE,"E13")}),1.0]])]});
            var Q23;
            Q23=makeQuery(id+"F0.imprint","IMPRINT",FACE,{"disambiguationData":[TD([[makeQuery(id+"F0.imprint","IMPRINT",EDGE,{"derivedFrom":sQuery(id+"F0.wireOp",EDGE,"E16")}),1.0]])]});
            var Q24;
            {var subQ0=sQuery(id+"F0.wireOp",EDGE,"E18");var subQ1=sQuery(id+"F0.wireOp",EDGE,"E14");var subQ2=makeQuery(id+"F0.imprint","INTERSECT",VERTEX,{"derivedFrom":[subQ1,subQ0]});Q24=makeQuery(id+"F0.imprint","IMPRINT",FACE,{"disambiguationData":[TD([[makeQuery(id+"F0.imprint","IMPRINT",EDGE,{"disambiguationData":[TD([[subQ2,1.0]])],"derivedFrom":subQ1}),-1.0]])]});}
            var Q25;
            {var subQ0=sQuery(id+"F0.wireOp",EDGE,"E21");var subQ1=sQuery(id+"F0.wireOp",EDGE,"E15");var subQ2=makeQuery(id+"F0.imprint","INTERSECT",VERTEX,{"derivedFrom":[subQ1,subQ0]});Q25=makeQuery(id+"F0.imprint","IMPRINT",FACE,{"disambiguationData":[TD([[makeQuery(id+"F0.imprint","IMPRINT",EDGE,{"disambiguationData":[TD([[subQ2,-1.0]])],"derivedFrom":subQ1}),-1.0]])]});}
            var Q26;
            {var subQ0=sQuery(id+"F0.wireOp",EDGE,"E7");var subQ1=sQuery(id+"F0.wireOp",EDGE,"s6BABxoF-F3zb-I8wc-I3Xw-FraqOPEOQCRA");var subQ2=makeQuery(id+"F0.imprint","INTERSECT",VERTEX,{"disambiguationData":[OD(1.0)],"derivedFrom":[subQ1,subQ0]});Q26=makeQuery(id+"F0.imprint","IMPRINT",FACE,{"disambiguationData":[TD([[makeQuery(id+"F0.imprint","IMPRINT",EDGE,{"disambiguationData":[TD([[subQ2,-1.0]])],"derivedFrom":subQ1}),1.0]])]});}
            var Q27;
            {var subQ0=sQuery(id+"F0.wireOp",EDGE,"4DxKJybv-C30h-320a-3xep-DEUsh5wGbbXE");var subQ1=sQuery(id+"F0.wireOp",EDGE,"E7");var subQ2=makeQuery(id+"F0.imprint","INTERSECT",VERTEX,{"disambiguationData":[OD(0.0)],"derivedFrom":[subQ1,subQ0]});Q27=makeQuery(id+"F0.imprint","IMPRINT",FACE,{"disambiguationData":[TD([[makeQuery(id+"F0.imprint","IMPRINT",EDGE,{"disambiguationData":[TD([[subQ2,1.0]])],"derivedFrom":subQ1}),1.0]])]});}
            var Q28;
            {var subQ0=sQuery(id+"F0.wireOp",EDGE,"E18");var subQ1=sQuery(id+"F0.wireOp",EDGE,"E5");var subQ2=makeQuery(id+"F0.imprint","INTERSECT",VERTEX,{"derivedFrom":[subQ1,subQ0]});Q28=makeQuery(id+"F0.imprint","IMPRINT",FACE,{"disambiguationData":[TD([[makeQuery(id+"F0.imprint","IMPRINT",EDGE,{"disambiguationData":[TD([[subQ2,-1.0]])],"derivedFrom":subQ1}),-1.0]])]});}
            var Q29;
            {var subQ5=sQuery(id+"F0.wireOp",EDGE,"E19");var subQ6=sQuery(id+"F0.wireOp",EDGE,"E8");var subQ7=makeQuery(id+"F0.imprint","INTERSECT",VERTEX,{"derivedFrom":[subQ6,subQ5]});Q29=makeQuery(id+"F0.imprint","IMPRINT",FACE,{"disambiguationData":[TD([[makeQuery(id+"F0.imprint","IMPRINT",EDGE,{"disambiguationData":[TD([[subQ7,-1.0]])],"derivedFrom":subQ6}),-1.0]])]});}
            var Q30;
            {var subQ0=sQuery(id+"F0.wireOp",EDGE,"E23");Q30=makeQuery(id+"F0.imprint","IMPRINT",FACE,{"disambiguationData":[TD([[makeQuery(id+"F0.imprint","IMPRINT",EDGE,{"derivedFrom":subQ0}),1.0]])]});}
            var Q31;
            {var subQ5=sQuery(id+"F0.wireOp",EDGE,"E17");var subQ7=sQuery(id+"F0.wireOp",EDGE,"E11");var subQ8=makeQuery(id+"F0.imprint","INTERSECT",VERTEX,{"derivedFrom":[subQ7,subQ5]});Q31=makeQuery(id+"F0.imprint","IMPRINT",FACE,{"disambiguationData":[TD([[makeQuery(id+"F0.imprint","IMPRINT",EDGE,{"disambiguationData":[TD([[subQ8,1.0]])],"derivedFrom":subQ7}),-1.0]])]});}
            var Q32;
            {var subQ3=sQuery(id+"F0.wireOp",EDGE,"E32");Q32=makeQuery(id+"F0.imprint","IMPRINT",FACE,{"disambiguationData":[TD([[makeQuery(id+"F0.imprint","IMPRINT",EDGE,{"derivedFrom":subQ3}),-1.0]])]});}
            var Q33;
            {var subQ1=sQuery(id+"F0.wireOp",EDGE,"E8");var subQ5=makeQuery(id+"F0.imprint","INTERSECT",VERTEX,{"derivedFrom":[subQ1,sQuery(id+"F0.wireOp",EDGE,"E19")]});Q33=makeQuery(id+"F0.imprint","IMPRINT",FACE,{"disambiguationData":[TD([[makeQuery(id+"F0.imprint","IMPRINT",EDGE,{"disambiguationData":[TD([[subQ5,1.0]])],"derivedFrom":subQ1}),1.0]])]});}
            var Q34;
            {var subQ3=sQuery(id+"F0.wireOp",EDGE,"E26");Q34=makeQuery(id+"F0.imprint","IMPRINT",FACE,{"disambiguationData":[TD([[makeQuery(id+"F0.imprint","IMPRINT",EDGE,{"derivedFrom":subQ3}),-1.0]])]});}
            var Q35;
            {var subQ0=sQuery(id+"F0.wireOp",EDGE,"E34");var subQ1=sQuery(id+"F0.wireOp",EDGE,"E33");var subQ2=makeQuery(id+"F0.imprint","INTERSECT",VERTEX,{"derivedFrom":[subQ1,subQ0]});Q35=makeQuery(id+"F0.imprint","IMPRINT",FACE,{"disambiguationData":[TD([[makeQuery(id+"F0.imprint","IMPRINT",EDGE,{"disambiguationData":[TD([[subQ2,1.0]])],"derivedFrom":subQ1}),-1.0]])]});}
            var Q36;
            {var subQ3=sQuery(id+"F0.wireOp",EDGE,"E27");Q36=makeQuery(id+"F0.imprint","IMPRINT",FACE,{"disambiguationData":[TD([[makeQuery(id+"F0.imprint","IMPRINT",EDGE,{"derivedFrom":subQ3}),1.0]])]});}
            var Q37;
            {var subQ0=sQuery(id+"F0.wireOp",EDGE,"E29");Q37=makeQuery(id+"F0.imprint","IMPRINT",FACE,{"disambiguationData":[TD([[makeQuery(id+"F0.imprint","IMPRINT",EDGE,{"derivedFrom":subQ0}),-1.0]])]});}
            var Q38;
            {var subQ0=sQuery(id+"F0.wireOp",EDGE,"E27");Q38=makeQuery(id+"F0.imprint","IMPRINT",FACE,{"disambiguationData":[TD([[makeQuery(id+"F0.imprint","IMPRINT",EDGE,{"derivedFrom":subQ0}),-1.0]])]});}
            var Q39;
            {var subQ0=sQuery(id+"F0.wireOp",EDGE,"E31");Q39=makeQuery(id+"F0.imprint","IMPRINT",FACE,{"disambiguationData":[TD([[makeQuery(id+"F0.imprint","IMPRINT",EDGE,{"derivedFrom":subQ0}),-1.0]])]});}
            var Q40;
            Q40=makeQuery(id+"F0.imprint","IMPRINT",FACE,{"disambiguationData":[TD([[makeQuery(id+"F0.imprint","IMPRINT",EDGE,{"derivedFrom":sQuery(id+"F0.wireOp",EDGE,"E7")}),-1.0]])]});
            var Q41;
            Q41=makeQuery(id+"F0.imprint","IMPRINT",FACE,{"disambiguationData":[TD([[makeQuery(id+"F0.imprint","IMPRINT",EDGE,{"derivedFrom":sQuery(id+"F0.wireOp",EDGE,"E13")}),-1.0]])]});
            var Q42;
            Q42=makeQuery(id+"F0.imprint","IMPRINT",FACE,{"disambiguationData":[TD([[makeQuery(id+"F0.imprint","IMPRINT",EDGE,{"derivedFrom":sQuery(id+"F0.wireOp",EDGE,"E16")}),-1.0]])]});
            extrude(context, id + "F3", {"entities" : qUnion([Q0, Q1, Q2, Q3, Q4, Q5, Q6, Q7, Q8, Q9, Q10, Q11, Q12, Q13, Q14, Q15, Q16, Q17, Q18, Q19, Q20, Q21, Q22, Q23, Q24, Q25, Q26, Q27, Q28, Q29, Q30, Q31, Q32, Q33, Q34, Q35, Q36, Q37, Q38, Q39, Q40, Q41, Q42]), "operationType" : NewBodyOperationType.ADD, "oppositeDirection" : true, "depth" : 11 * mm, "offsetDistance" : 25 * mm});
        }
        {
            var Q0;
            {var subQ0=sQuery(id+"F0.wireOp",EDGE,"E6");var subQ1=sQuery(id+"F0.wireOp",EDGE,"E1");var subQ2=makeQuery(id+"F0.imprint","INTERSECT",VERTEX,{"derivedFrom":[subQ1,subQ0]});Q0=makeQuery(id+"F0.imprint","IMPRINT",FACE,{"disambiguationData":[TD([[makeQuery(id+"F0.imprint","IMPRINT",EDGE,{"disambiguationData":[TD([[subQ2,-1.0]])],"derivedFrom":subQ1}),-1.0]])]});}
            var Q1;
            {var subQ0=sQuery(id+"F0.wireOp",EDGE,"E9");var subQ1=sQuery(id+"F0.wireOp",EDGE,"E3");var subQ2=makeQuery(id+"F0.imprint","INTERSECT",VERTEX,{"derivedFrom":[subQ1,subQ0]});Q1=makeQuery(id+"F0.imprint","IMPRINT",FACE,{"disambiguationData":[TD([[makeQuery(id+"F0.imprint","IMPRINT",EDGE,{"disambiguationData":[TD([[subQ2,-1.0]])],"derivedFrom":subQ1}),-1.0]])]});}
            var Q2;
            {var subQ0=sQuery(id+"F0.wireOp",EDGE,"E12");var subQ1=sQuery(id+"F0.wireOp",EDGE,"E2");var subQ2=makeQuery(id+"F0.imprint","INTERSECT",VERTEX,{"derivedFrom":[subQ1,subQ0]});Q2=makeQuery(id+"F0.imprint","IMPRINT",FACE,{"disambiguationData":[TD([[makeQuery(id+"F0.imprint","IMPRINT",EDGE,{"disambiguationData":[TD([[subQ2,-1.0]])],"derivedFrom":subQ1}),-1.0]])]});}
            var Q3;
            {var subQ2=sQuery(id+"F0.wireOp",EDGE,"E17");var subQ7=sQuery(id+"F0.wireOp",EDGE,"E14");var subQ8=makeQuery(id+"F0.imprint","INTERSECT",VERTEX,{"derivedFrom":[subQ7,subQ2]});Q3=makeQuery(id+"F0.imprint","IMPRINT",FACE,{"disambiguationData":[TD([[makeQuery(id+"F0.imprint","IMPRINT",EDGE,{"disambiguationData":[TD([[subQ8,1.0]])],"derivedFrom":subQ7}),-1.0]])]});}
            var Q4;
            {var subQ5=sQuery(id+"F0.wireOp",EDGE,"E18");var subQ7=sQuery(id+"F0.wireOp",EDGE,"E5");var subQ8=makeQuery(id+"F0.imprint","INTERSECT",VERTEX,{"derivedFrom":[subQ7,subQ5]});Q4=makeQuery(id+"F0.imprint","IMPRINT",FACE,{"disambiguationData":[TD([[makeQuery(id+"F0.imprint","IMPRINT",EDGE,{"disambiguationData":[TD([[subQ8,1.0]])],"derivedFrom":subQ7}),-1.0]])]});}
            var Q5;
            {var subQ0=sQuery(id+"F0.wireOp",EDGE,"E15");var subQ1=sQuery(id+"F0.wireOp",EDGE,"E4");var subQ2=makeQuery(id+"F0.imprint","INTERSECT",VERTEX,{"derivedFrom":[subQ1,subQ0]});Q5=makeQuery(id+"F0.imprint","IMPRINT",FACE,{"disambiguationData":[TD([[makeQuery(id+"F0.imprint","IMPRINT",EDGE,{"disambiguationData":[TD([[subQ2,-1.0]])],"derivedFrom":subQ1}),-1.0]])]});}
            var Q6;
            {var subQ5=sQuery(id+"F0.wireOp",EDGE,"E8");var subQ7=sQuery(id+"F0.wireOp",EDGE,"E19");var subQ9=makeQuery(id+"F0.imprint","INTERSECT",VERTEX,{"derivedFrom":[subQ5,subQ7]});Q6=makeQuery(id+"F0.imprint","IMPRINT",FACE,{"disambiguationData":[TD([[makeQuery(id+"F0.imprint","IMPRINT",EDGE,{"disambiguationData":[TD([[subQ9,1.0]])],"derivedFrom":subQ5}),-1.0]])]});}
            var Q7;
            {var subQ3=sQuery(id+"F0.wireOp",EDGE,"E17");var subQ4=sQuery(id+"F0.wireOp",EDGE,"E11");var subQ5=makeQuery(id+"F0.imprint","INTERSECT",VERTEX,{"derivedFrom":[subQ4,subQ3]});Q7=makeQuery(id+"F0.imprint","IMPRINT",FACE,{"disambiguationData":[TD([[makeQuery(id+"F0.imprint","IMPRINT",EDGE,{"disambiguationData":[TD([[subQ5,-1.0]])],"derivedFrom":subQ4}),-1.0]])]});}
            extrude(context, id + "F4", {"entities" : qUnion([Q0, Q1, Q2, Q3, Q4, Q5, Q6, Q7]), "oppositeDirection" : true, "depth" : 11 * mm, "offsetDistance" : 25 * mm});
        }
        {
            var Q0;
            Q0=qCreatedBy(makeId("Right.planeOp"),FACE);
            var sketch = newSketch(context, id + "F5", { "sketchPlane" : qUnion([Q0])});
            skLineSegment(sketch, "E38.0.0", {"start": v(-15, 8) * mm, "end": v(-15, -21.2) * mm});
            skLineSegment(sketch, "E38.0.1", {"start": v(-15, -21.2) * mm, "end": v(15, -21.2) * mm});
            skLineSegment(sketch, "E38.0.2", {"start": v(15, -21.2) * mm, "end": v(15, 8) * mm});
            skLineSegment(sketch, "E38.0.3", {"start": v(15, 8) * mm, "end": v(-15, 8) * mm});
            skLineSegment(sketch, "E39", {"start": v(-15, -1.5) * mm, "end": v(15, -12.12) * mm});
            skLineSegment(sketch, "E40", {"start": v(-15, 0) * mm, "end": v(15, -10.62) * mm});
            skLineSegment(sketch, "E41.0", {"start": v(-11, -21.2) * mm, "end": v(-11, 0) * mm, "construction": true});
            skLineSegment(sketch, "E42.0", {"start": v(12.82, -21.2) * mm, "end": v(12.82, 0) * mm, "construction": true});
            skLineSegment(sketch, "E43", {"start": v(-11, -2.92) * mm, "end": v(-15, -2.92) * mm});
            skLineSegment(sketch, "E44", {"start": v(12.82, -9.85) * mm, "end": v(15, -9.85) * mm});
            skLineSegment(sketch, "E45", {"start": v(-15, 0) * mm, "end": v(15, 0) * mm});
            skLineSegment(sketch, "E46", {"start": v(12.82, -11.35) * mm, "end": v(15, -11.35) * mm});
            skLineSegment(sketch, "E47", {"start": v(-15, -1.42) * mm, "end": v(-11, -1.42) * mm});
            skPoint(sketch, "E48.0", {"position": v(-11, 0) * mm});
            skPoint(sketch, "E48.1", {"position": v(-11, 0) * mm});
            skPoint(sketch, "E49.0", {"position": v(12.82, 0) * mm});
            skSolve(sketch);
        }
        {
            var Q0;
            {var subQ4=sQuery(id+"F5.wireOp",EDGE,"E38.0.1");Q0=makeQuery(id+"F5.imprint","IMPRINT",FACE,{"disambiguationData":[TD([[makeQuery(id+"F5.imprint","IMPRINT",EDGE,{"derivedFrom":subQ4}),1.0]])]});}
            var Q1;
            {var subQ3=sQuery(id+"F5.wireOp",EDGE,"hunu5mRh-pqae-i8tr-iFnI-zPmTSEyom6et");Q1=makeQuery(id+"F5.imprint","IMPRINT",FACE,{"disambiguationData":[TD([[makeQuery(id+"F5.imprint","IMPRINT",EDGE,{"derivedFrom":subQ3}),-1.0]])]});}
            var Q2;
            {var subQ0=sQuery(id+"F5.wireOp",EDGE,"5obCXoEq-Wm3H-brtq-ZrH3-ew40qmmA4Y0c");Q2=makeQuery(id+"F5.imprint","IMPRINT",FACE,{"disambiguationData":[TD([[makeQuery(id+"F5.imprint","IMPRINT",EDGE,{"derivedFrom":subQ0}),-1.0]])]});}
            var Q3;
            {var subQ0=sQuery(id+"F5.wireOp",EDGE,"E39");var subQ1=sQuery(id+"F5.wireOp",EDGE,"E38.0.2");var subQ2=makeQuery(id+"F5.imprint","INTERSECT",VERTEX,{"derivedFrom":[subQ1,subQ0]});Q3=makeQuery(id+"F5.imprint","IMPRINT",FACE,{"disambiguationData":[TD([[makeQuery(id+"F5.imprint","IMPRINT",EDGE,{"disambiguationData":[TD([[subQ2,-1.0]])],"derivedFrom":subQ1}),1.0]])]});}
            extrude(context, id + "F6", {"entities" : qUnion([Q0, Q1, Q2, Q3]), "operationType" : NewBodyOperationType.REMOVE, "endBound" : BoundingType.THROUGH_ALL, "oppositeDirection" : true, "depth" : 25 * mm, "offsetDistance" : 25 * mm, "hasSecondDirection" : true, "secondDirectionBound" : BoundingType.THROUGH_ALL, "secondDirectionOppositeDirection" : false, "secondDirectionDepth" : 25 * mm});
        }
        {
            var Q0;
            {var subQ0=sQuery(id+"F5.wireOp",EDGE,"DL6gxKGO-Bxk7-75Pn-TxgM-fMXyvmIIm4l2");var subQ1=sQuery(id+"F5.wireOp",EDGE,"E39");var subQ2=makeQuery(id+"F5.imprint","INTERSECT",VERTEX,{"derivedFrom":[subQ1,sQuery(id+"F5.wireOp",EDGE,"E43"),subQ0]});Q0=makeQuery(id+"F5.imprint","IMPRINT",FACE,{"disambiguationData":[TD([[makeQuery(id+"F5.imprint","IMPRINT",EDGE,{"disambiguationData":[TD([[subQ2,-1.0]])],"derivedFrom":subQ1}),1.0]])]});}
            var Q1;
            {var subQ0=sQuery(id+"F5.wireOp",EDGE,"b2AHApLv-iO4g-mdL0-7SMa-YLQOZYVEnQ83");Q1=makeQuery(id+"F5.imprint","IMPRINT",FACE,{"disambiguationData":[TD([[makeQuery(id+"F5.imprint","IMPRINT",EDGE,{"derivedFrom":subQ0}),1.0]])]});}
            var Q2;
            {var subQ0=sQuery(id+"F5.wireOp",EDGE,"hunu5mRh-pqae-i8tr-iFnI-zPmTSEyom6et");Q2=makeQuery(id+"F5.imprint","IMPRINT",FACE,{"disambiguationData":[TD([[makeQuery(id+"F5.imprint","IMPRINT",EDGE,{"derivedFrom":subQ0}),1.0]])]});}
            var Q3;
            {var subQ0=sQuery(id+"F5.wireOp",EDGE,"5obCXoEq-Wm3H-brtq-ZrH3-ew40qmmA4Y0c");Q3=makeQuery(id+"F5.imprint","IMPRINT",FACE,{"disambiguationData":[TD([[makeQuery(id+"F5.imprint","IMPRINT",EDGE,{"derivedFrom":subQ0}),1.0]])]});}
            var Q4;
            {var subQ3=sQuery(id+"F5.wireOp",EDGE,"E43");Q4=makeQuery(id+"F5.imprint","IMPRINT",FACE,{"disambiguationData":[TD([[makeQuery(id+"F5.imprint","IMPRINT",EDGE,{"derivedFrom":subQ3}),-1.0]])]});}
            var Q5;
            {var subQ0=sQuery(id+"F5.wireOp",EDGE,"E44");Q5=makeQuery(id+"F5.imprint","IMPRINT",FACE,{"disambiguationData":[TD([[makeQuery(id+"F5.imprint","IMPRINT",EDGE,{"derivedFrom":subQ0}),-1.0]])]});}
            extrude(context, id + "F7", {"entities" : qUnion([Q0, Q1, Q2, Q3, Q4, Q5]), "operationType" : NewBodyOperationType.REMOVE, "endBound" : BoundingType.THROUGH_ALL, "oppositeDirection" : true, "depth" : 25 * mm, "offsetDistance" : 25 * mm, "hasSecondDirection" : true, "secondDirectionBound" : BoundingType.THROUGH_ALL, "secondDirectionOppositeDirection" : false, "secondDirectionDepth" : 25 * mm});
        }
        {
            var Q0;
            {var subQ0=sQuery(id+"F0.wireOp",EDGE,"E5");var subQ1=sQuery(id+"F0.wireOp",EDGE,"s6BABxoF-F3zb-I8wc-I3Xw-FraqOPEOQCRA");var subQ2=makeQuery(id+"F0.imprint","INTERSECT",VERTEX,{"disambiguationData":[OD(0.0)],"derivedFrom":[subQ1,subQ0]});Q0=makeQuery(id+"F0.imprint","IMPRINT",FACE,{"disambiguationData":[TD([[makeQuery(id+"F0.imprint","IMPRINT",EDGE,{"disambiguationData":[TD([[subQ2,-1.0]])],"derivedFrom":subQ1}),1.0]])]});}
            var Q1;
            {var subQ0=sQuery(id+"F0.wireOp",EDGE,"E5");var subQ1=sQuery(id+"F0.wireOp",EDGE,"s6BABxoF-F3zb-I8wc-I3Xw-FraqOPEOQCRA");var subQ2=makeQuery(id+"F0.imprint","INTERSECT",VERTEX,{"disambiguationData":[OD(0.0)],"derivedFrom":[subQ1,subQ0]});Q1=makeQuery(id+"F0.imprint","IMPRINT",FACE,{"disambiguationData":[TD([[makeQuery(id+"F0.imprint","IMPRINT",EDGE,{"disambiguationData":[TD([[subQ2,-1.0]])],"derivedFrom":subQ1}),-1.0]])]});}
            var Q2;
            Q2=makeQuery(id+"F0.imprint","IMPRINT",FACE,{"disambiguationData":[TD([[makeQuery(id+"F0.imprint","IMPRINT",EDGE,{"derivedFrom":sQuery(id+"F0.wireOp",EDGE,"E14")}),1.0]])]});
            var Q3;
            {var subQ1=sQuery(id+"F0.wireOp",EDGE,"E5");var subQ5=makeQuery(id+"F0.imprint","INTERSECT",VERTEX,{"derivedFrom":[subQ1,sQuery(id+"F0.wireOp",EDGE,"E18")]});Q3=makeQuery(id+"F0.imprint","IMPRINT",FACE,{"disambiguationData":[TD([[makeQuery(id+"F0.imprint","IMPRINT",EDGE,{"disambiguationData":[TD([[subQ5,1.0]])],"derivedFrom":subQ1}),1.0]])]});}
            var Q4;
            {var subQ0=sQuery(id+"F0.wireOp",EDGE,"E7");var subQ1=sQuery(id+"F0.wireOp",EDGE,"s6BABxoF-F3zb-I8wc-I3Xw-FraqOPEOQCRA");var subQ2=makeQuery(id+"F0.imprint","INTERSECT",VERTEX,{"disambiguationData":[OD(1.0)],"derivedFrom":[subQ1,subQ0]});Q4=makeQuery(id+"F0.imprint","IMPRINT",FACE,{"disambiguationData":[TD([[makeQuery(id+"F0.imprint","IMPRINT",EDGE,{"disambiguationData":[TD([[subQ2,-1.0]])],"derivedFrom":subQ1}),1.0]])]});}
            var Q5;
            Q5=makeQuery(id+"F0.imprint","IMPRINT",FACE,{"disambiguationData":[TD([[makeQuery(id+"F0.imprint","IMPRINT",EDGE,{"derivedFrom":sQuery(id+"F0.wireOp",EDGE,"E16")}),-1.0]])]});
            extrude(context, id + "F8", {"entities" : qUnion([Q0, Q1, Q2, Q3, Q4, Q5]), "operationType" : NewBodyOperationType.REMOVE, "endBound" : BoundingType.THROUGH_ALL, "depth" : 25 * mm, "offsetDistance" : 25 * mm, "hasSecondDirection" : true, "secondDirectionOppositeDirection" : false, "secondDirectionDepth" : 2 * mm});
        }
        {
            var Q0;
            Q0=makeQuery(id+"F0.imprint","IMPRINT",FACE,{"disambiguationData":[TD([[makeQuery(id+"F0.imprint","IMPRINT",EDGE,{"derivedFrom":sQuery(id+"F0.wireOp",EDGE,"E13")}),-1.0]])]});
            var Q1;
            {var subQ0=sQuery(id+"F0.wireOp",EDGE,"E11");var subQ1=sQuery(id+"F0.wireOp",EDGE,"MlNcj02m-OnEw-u7mJ-xsQt-vaGhrOIsEcpA");var subQ2=makeQuery(id+"F0.imprint","INTERSECT",VERTEX,{"disambiguationData":[OD(0.0)],"derivedFrom":[subQ1,subQ0]});Q1=makeQuery(id+"F0.imprint","IMPRINT",FACE,{"disambiguationData":[TD([[makeQuery(id+"F0.imprint","IMPRINT",EDGE,{"disambiguationData":[TD([[subQ2,-1.0]])],"derivedFrom":subQ1}),1.0]])]});}
            extrude(context, id + "F9", {"entities" : qUnion([Q0, Q1]), "operationType" : NewBodyOperationType.REMOVE, "depth" : 25 * mm, "offsetDistance" : 25 * mm, "hasSecondDirection" : true, "secondDirectionOppositeDirection" : true, "secondDirectionDepth" : 5.5 * mm});
        }
        {
            var Q0;
            {var subQ1=sQuery(id+"F0.wireOp",EDGE,"E1");var subQ3=sQuery(id+"F0.wireOp",EDGE,"E9");var subQ4=makeQuery(id+"F0.imprint","INTERSECT",VERTEX,{"derivedFrom":[subQ1,subQ3]});Q0=makeQuery(id+"F0.imprint","IMPRINT",FACE,{"disambiguationData":[TD([[makeQuery(id+"F0.imprint","IMPRINT",EDGE,{"disambiguationData":[TD([[subQ4,1.0]])],"derivedFrom":subQ3}),-1.0]])]});}
            var Q1;
            {var subQ1=sQuery(id+"F0.wireOp",EDGE,"E3");var subQ3=sQuery(id+"F0.wireOp",EDGE,"E9");var subQ4=makeQuery(id+"F0.imprint","INTERSECT",VERTEX,{"derivedFrom":[subQ1,subQ3]});Q1=makeQuery(id+"F0.imprint","IMPRINT",FACE,{"disambiguationData":[TD([[makeQuery(id+"F0.imprint","IMPRINT",EDGE,{"disambiguationData":[TD([[subQ4,-1.0]])],"derivedFrom":subQ3}),-1.0]])]});}
            var Q2;
            {var subQ1=sQuery(id+"F0.wireOp",EDGE,"E4");var subQ3=sQuery(id+"F0.wireOp",EDGE,"E6");var subQ4=makeQuery(id+"F0.imprint","INTERSECT",VERTEX,{"derivedFrom":[subQ1,subQ3]});Q2=makeQuery(id+"F0.imprint","IMPRINT",FACE,{"disambiguationData":[TD([[makeQuery(id+"F0.imprint","IMPRINT",EDGE,{"disambiguationData":[TD([[subQ4,1.0]])],"derivedFrom":subQ3}),-1.0]])]});}
            var Q3;
            {var subQ1=sQuery(id+"F0.wireOp",EDGE,"E1");var subQ3=sQuery(id+"F0.wireOp",EDGE,"E6");var subQ4=makeQuery(id+"F0.imprint","INTERSECT",VERTEX,{"derivedFrom":[subQ1,subQ3]});Q3=makeQuery(id+"F0.imprint","IMPRINT",FACE,{"disambiguationData":[TD([[makeQuery(id+"F0.imprint","IMPRINT",EDGE,{"disambiguationData":[TD([[subQ4,-1.0]])],"derivedFrom":subQ3}),-1.0]])]});}
            var Q4;
            {var subQ0=sQuery(id+"F0.wireOp",EDGE,"E7");var subQ1=sQuery(id+"F0.wireOp",EDGE,"s6BABxoF-F3zb-I8wc-I3Xw-FraqOPEOQCRA");var subQ2=makeQuery(id+"F0.imprint","INTERSECT",VERTEX,{"disambiguationData":[OD(0.0)],"derivedFrom":[subQ1,subQ0]});Q4=makeQuery(id+"F0.imprint","IMPRINT",FACE,{"disambiguationData":[TD([[makeQuery(id+"F0.imprint","IMPRINT",EDGE,{"disambiguationData":[TD([[subQ2,-1.0]])],"derivedFrom":subQ1}),1.0]])]});}
            var Q5;
            {var subQ0=sQuery(id+"F0.wireOp",EDGE,"E7");var subQ1=sQuery(id+"F0.wireOp",EDGE,"s6BABxoF-F3zb-I8wc-I3Xw-FraqOPEOQCRA");var subQ2=makeQuery(id+"F0.imprint","INTERSECT",VERTEX,{"disambiguationData":[OD(0.0)],"derivedFrom":[subQ1,subQ0]});Q5=makeQuery(id+"F0.imprint","IMPRINT",FACE,{"disambiguationData":[TD([[makeQuery(id+"F0.imprint","IMPRINT",EDGE,{"disambiguationData":[TD([[subQ2,-1.0]])],"derivedFrom":subQ1}),-1.0]])]});}
            var Q6;
            Q6=makeQuery(id+"F0.imprint","IMPRINT",FACE,{"disambiguationData":[TD([[makeQuery(id+"F0.imprint","IMPRINT",EDGE,{"derivedFrom":sQuery(id+"F0.wireOp",EDGE,"E16")}),1.0]])]});
            var Q7;
            {var subQ0=sQuery(id+"F0.wireOp",EDGE,"E4");var subQ1=sQuery(id+"F0.wireOp",EDGE,"E2");var subQ2=makeQuery(id+"F0.imprint","INTERSECT",VERTEX,{"derivedFrom":[subQ1,subQ0]});Q7=makeQuery(id+"F0.imprint","IMPRINT",FACE,{"disambiguationData":[TD([[makeQuery(id+"F0.imprint","IMPRINT",EDGE,{"disambiguationData":[TD([[subQ2,1.0]])],"derivedFrom":subQ1}),-1.0]])]});}
            var Q8;
            Q8=makeQuery(id+"F0.imprint","IMPRINT",FACE,{"disambiguationData":[TD([[makeQuery(id+"F0.imprint","IMPRINT",EDGE,{"derivedFrom":sQuery(id+"F0.wireOp",EDGE,"E13")}),1.0]])]});
            var Q9;
            {var subQ1=sQuery(id+"F0.wireOp",EDGE,"E2");var subQ3=sQuery(id+"F0.wireOp",EDGE,"E12");var subQ4=makeQuery(id+"F0.imprint","INTERSECT",VERTEX,{"derivedFrom":[subQ1,subQ3]});Q9=makeQuery(id+"F0.imprint","IMPRINT",FACE,{"disambiguationData":[TD([[makeQuery(id+"F0.imprint","IMPRINT",EDGE,{"disambiguationData":[TD([[subQ4,-1.0]])],"derivedFrom":subQ3}),-1.0]])]});}
            var Q10;
            {var subQ1=sQuery(id+"F0.wireOp",EDGE,"E3");var subQ3=sQuery(id+"F0.wireOp",EDGE,"E12");var subQ4=makeQuery(id+"F0.imprint","INTERSECT",VERTEX,{"derivedFrom":[subQ1,subQ3]});Q10=makeQuery(id+"F0.imprint","IMPRINT",FACE,{"disambiguationData":[TD([[makeQuery(id+"F0.imprint","IMPRINT",EDGE,{"disambiguationData":[TD([[subQ4,1.0]])],"derivedFrom":subQ3}),-1.0]])]});}
            var Q11;
            {var subQ1=sQuery(id+"F0.wireOp",EDGE,"s6BABxoF-F3zb-I8wc-I3Xw-FraqOPEOQCRA");var subQ3=sQuery(id+"F0.wireOp",EDGE,"E6");var subQ4=makeQuery(id+"F0.imprint","INTERSECT",VERTEX,{"disambiguationData":[OD(1.0)],"derivedFrom":[subQ1,subQ3]});Q11=makeQuery(id+"F0.imprint","IMPRINT",FACE,{"disambiguationData":[TD([[makeQuery(id+"F0.imprint","IMPRINT",EDGE,{"disambiguationData":[TD([[subQ4,-1.0]])],"derivedFrom":subQ3}),-1.0]])]});}
            var Q12;
            {var subQ1=sQuery(id+"F0.wireOp",EDGE,"E4");var subQ3=sQuery(id+"F0.wireOp",EDGE,"E15");var subQ4=makeQuery(id+"F0.imprint","INTERSECT",VERTEX,{"derivedFrom":[subQ1,subQ3]});Q12=makeQuery(id+"F0.imprint","IMPRINT",FACE,{"disambiguationData":[TD([[makeQuery(id+"F0.imprint","IMPRINT",EDGE,{"disambiguationData":[TD([[subQ4,-1.0]])],"derivedFrom":subQ3}),-1.0]])]});}
            var Q13;
            {var subQ0=sQuery(id+"F0.wireOp",EDGE,"4DxKJybv-C30h-320a-3xep-DEUsh5wGbbXE");var subQ1=sQuery(id+"F0.wireOp",EDGE,"E7");var subQ2=makeQuery(id+"F0.imprint","INTERSECT",VERTEX,{"disambiguationData":[OD(0.0)],"derivedFrom":[subQ1,subQ0]});Q13=makeQuery(id+"F0.imprint","IMPRINT",FACE,{"disambiguationData":[TD([[makeQuery(id+"F0.imprint","IMPRINT",EDGE,{"disambiguationData":[TD([[subQ2,1.0]])],"derivedFrom":subQ1}),1.0]])]});}
            extrude(context, id + "F10", {"entities" : qUnion([Q0, Q1, Q2, Q3, Q4, Q5, Q6, Q7, Q8, Q9, Q10, Q11, Q12, Q13]), "operationType" : NewBodyOperationType.REMOVE, "endBound" : BoundingType.THROUGH_ALL, "oppositeDirection" : true, "depth" : 25 * mm, "offsetDistance" : 25 * mm, "hasSecondDirection" : true, "secondDirectionBound" : BoundingType.THROUGH_ALL, "secondDirectionOppositeDirection" : false, "secondDirectionDepth" : 25 * mm});
        }
    });
